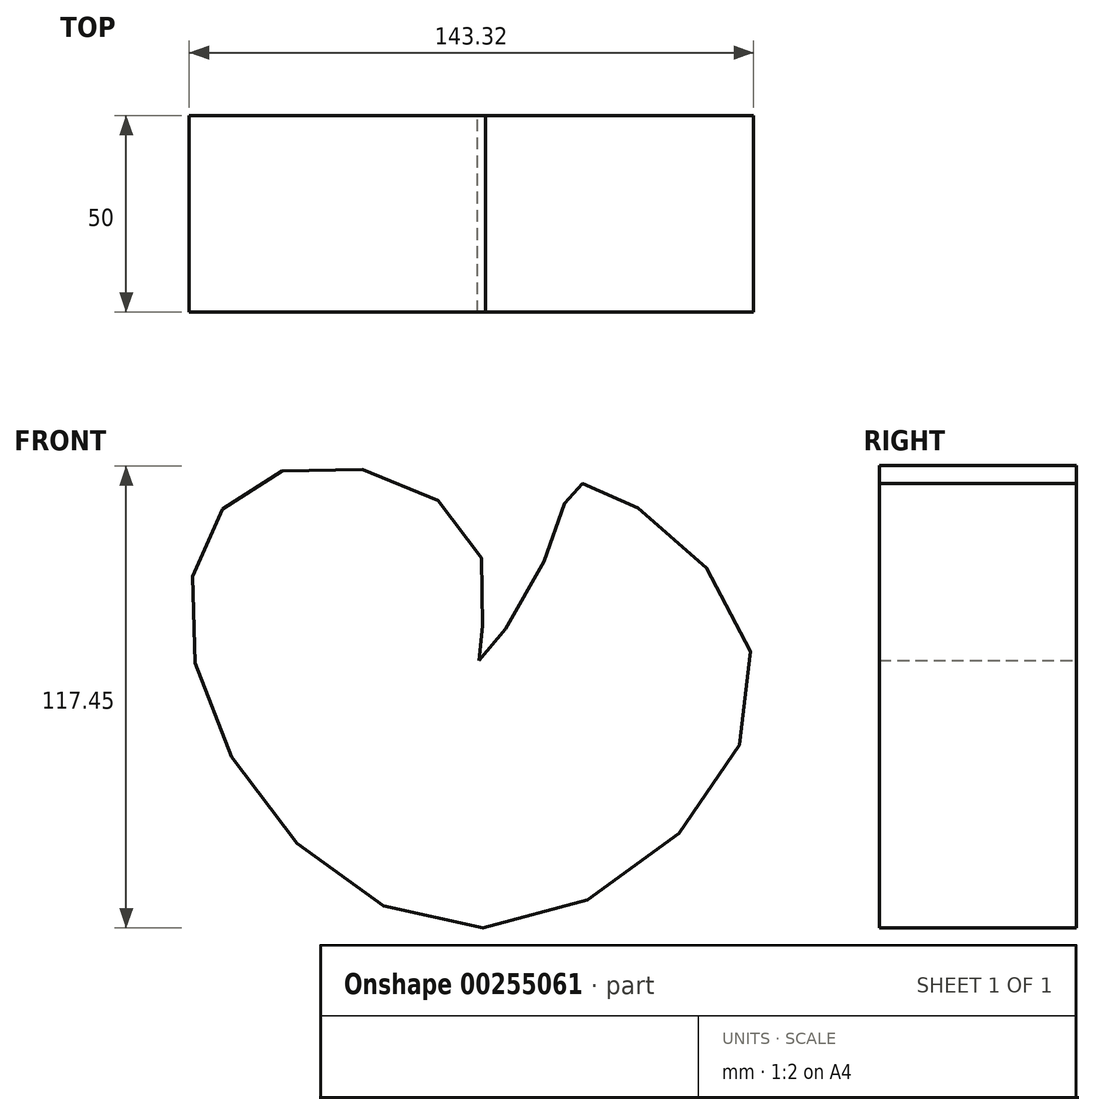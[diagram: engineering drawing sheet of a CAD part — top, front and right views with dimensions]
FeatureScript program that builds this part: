
annotation { "Feature Type Name" : "Feature", "Feature Type Description" : "" }
export const myFeature = defineFeature(function(context is Context, id is Id, definition is map)
    precondition{}
    {
        {
            var Q0;
            Q0=qCreatedBy(makeId("Front.planeOp"),FACE);
            var sketch = newSketch(context, id + "F0", { "sketchPlane" : qUnion([Q0])});
            skFitSpline(sketch, "E0", {"points": [v(0, 0) * mm, v(0, 28.05) * mm, v(-51.63, 47.63) * mm, v(-72.28, 0) * mm, v(0, -68) * mm, v(69.4, 0) * mm, v(25.73, 44.93) * mm, v(19.97, 33.4) * mm, v(0, 0) * mm]});
            skSolve(sketch);
        }
        {
            var Q0;
            Q0=makeQuery(id+"F0.imprint","IMPRINT",FACE,{"disambiguationData":[TD([[makeQuery(id+"F0.imprint","IMPRINT",EDGE,{"derivedFrom":sQuery(id+"F0.wireOp",EDGE,"E0")}),1.0]])]});
            extrude(context, id + "F1", {"entities" : qUnion([Q0]), "depth" : 50 * mm});
        }
    });
